# Revit family: QF_MOFFAT WALDORF_RN8910GC
name_source: partatom
category: Specialty Equipment
revit_build: Autodesk Revit Architecture 2012 (Build: 20110309_2315(x64)
units: mm (PartAtom-declared; Revit-internal decimal feet)

## types (1)
- QF_MOFFAT WALDORF_RN8910GC
    Apparent Power = 0 VA
    Body Finish = QF_Finishes_Stainless Steel
    Cold Water Connection Height = 0"
    Cold Water Flow = 0 GPM
    Cold Water Maximum Pressure = 0.00 psi
    Cold Water Minimum Pressure = 0.00 psi
    Cold Water Size = 1"
    Cold Water Temperature Recommended = -460 °F
    Conn Conduit = Yes
    Cycle = 50 Hz
    Depth = 31 11/16"
    Description = RANGE GAS WITH CONVECTION OVEN
    FL Amps = 0 A
    Gas Connection Height = 0"
    Gas Size = 1"
    Height = 44 1/2"
    Manufacturer = MOFFAT WALDORF
    Max Overcurrent Protection = 0 A
    Min Ckt Ampacity = 0 A
    Model = RN8910GC
    Phase = 1
    URL = www.moffat.com
    URL Cutsheet = www.moffat.com
    Volts = 240 V
    Watts = 130 W
    Weight in Pounds = 215
    Width = 35 7/16"

## geometry (parser evidence)
native form markers: Blend x5, Sweep x5
no freeform markers — native parametric forms only
